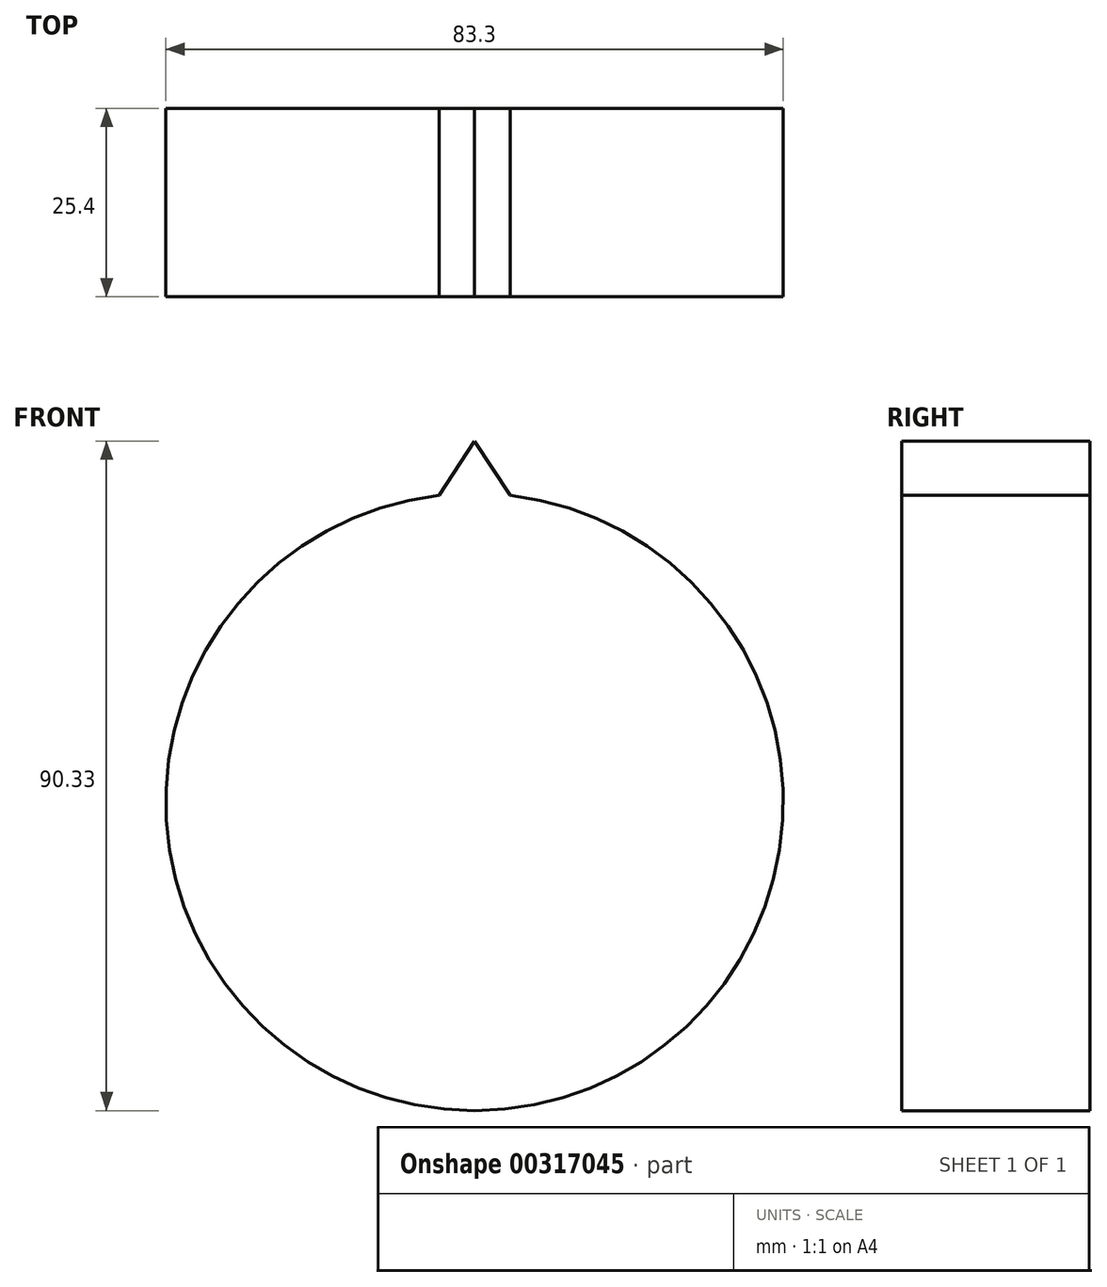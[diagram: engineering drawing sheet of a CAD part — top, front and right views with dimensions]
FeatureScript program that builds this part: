
annotation { "Feature Type Name" : "Feature", "Feature Type Description" : "" }
export const myFeature = defineFeature(function(context is Context, id is Id, definition is map)
    precondition{}
    {
        {
            var Q0;
            Q0=qCreatedBy(makeId("Front.planeOp"),FACE);
            var sketch = newSketch(context, id + "F0", { "sketchPlane" : qUnion([Q0])});
            skCircle(sketch, "E0", {"center": v(0, 0) * mm, "radius": 41.65 * mm});
            skSolve(sketch);
        }
        {
            var Q0;
            Q0 = qSketchRegion(id + "F0", true);
            extrude(context, id + "F1", {"entities" : qUnion([Q0]), "depth" : 25.4 * mm, "symmetric" : true});
        }
        {
            var Q0;
            Q0=makeQuery(id+"F1.opExtrude","CAP_FACE",FACE,{"disambiguationData":[OSD([sQuery(id+"F0.wireOp",EDGE,"E0")])],"isStart":false});
            var sketch = newSketch(context, id + "F2", { "sketchPlane" : qUnion([Q0])});
            skLineSegment(sketch, "E1", {"start": v(-4.8, 41.38) * mm, "end": v(0, 48.68) * mm});
            skLineSegment(sketch, "E2", {"start": v(0, 48.68) * mm, "end": v(4.8, 41.38) * mm});
            skSolve(sketch);
        }
        {
            var Q0;
            {var subQ0=sQuery(id+"F2.wireOp",EDGE,"E1");Q0=makeQuery(id+"F2.imprint","IMPRINT",FACE,{"disambiguationData":[TD([[makeQuery(id+"F2.imprint","IMPRINT",EDGE,{"derivedFrom":subQ0}),-1.0]])]});}
            var Q1;
            Q1=makeQuery(id+"F1.opExtrude","CAP_FACE",FACE,{"disambiguationData":[OSD([sQuery(id+"F0.wireOp",EDGE,"E0")])],"isStart":true});
            extrude(context, id + "F3", {"entities" : qUnion([Q0]), "operationType" : NewBodyOperationType.ADD, "endBound" : BoundingType.UP_TO_SURFACE, "oppositeDirection" : true, "endBoundEntityFace" : qUnion([Q1]), "depth" : 32.5 * mm});
        }
    });
